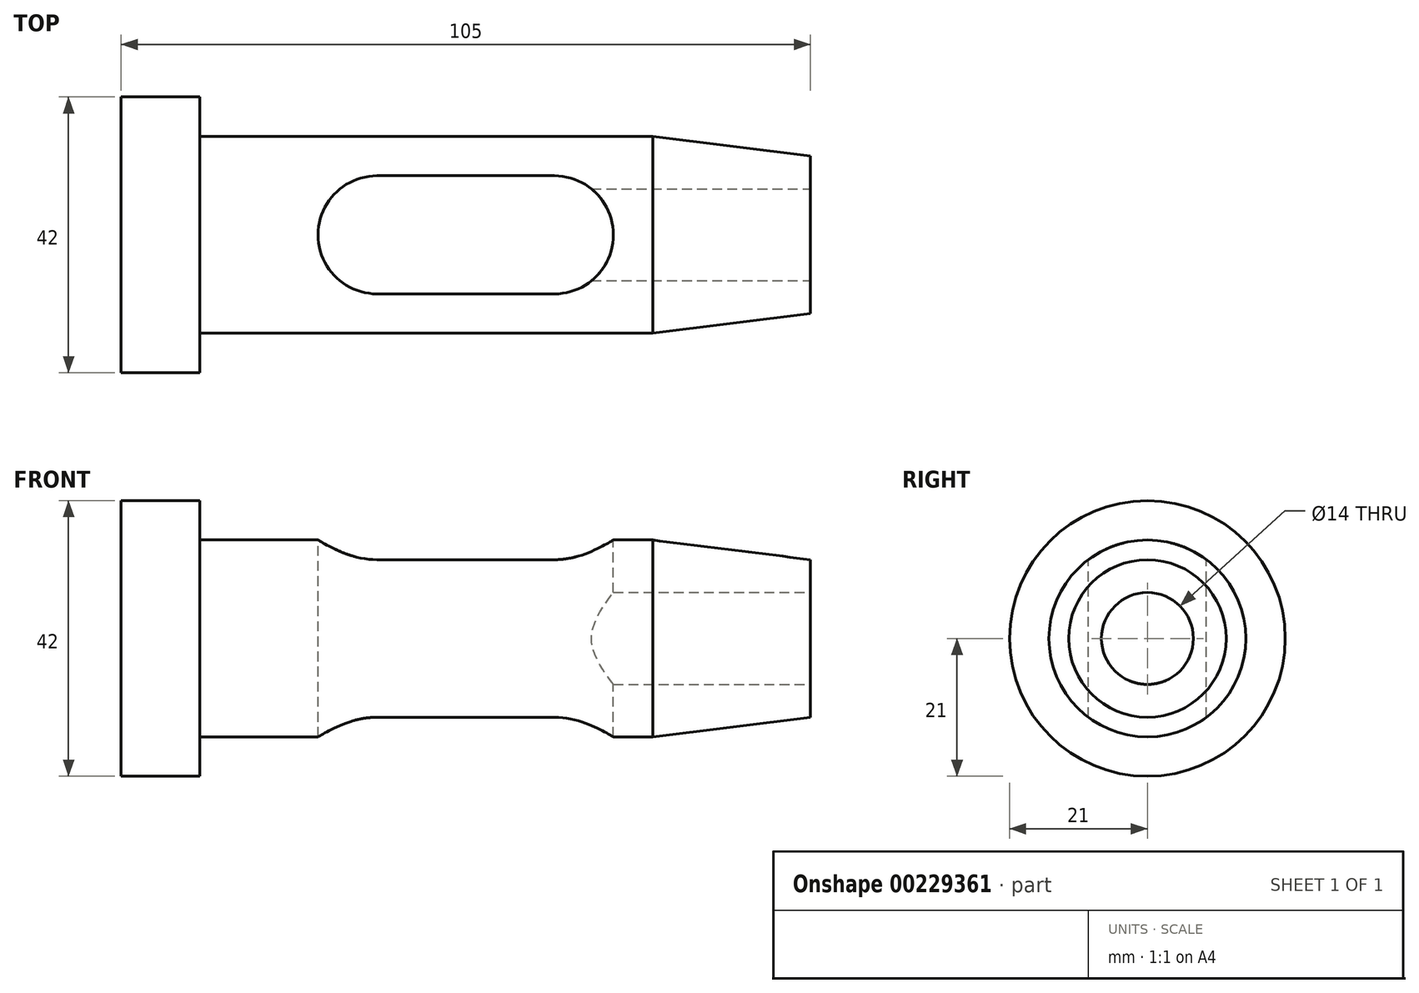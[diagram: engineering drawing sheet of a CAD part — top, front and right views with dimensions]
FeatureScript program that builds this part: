
annotation { "Feature Type Name" : "Feature", "Feature Type Description" : "" }
export const myFeature = defineFeature(function(context is Context, id is Id, definition is map)
    precondition{}
    {
        {
            var Q0;
            Q0=qCreatedBy(makeId("Front.planeOp"),FACE);
            var sketch = newSketch(context, id + "F0", { "sketchPlane" : qUnion([Q0])});
            skLineSegment(sketch, "E0", {"start": v(-105, 0) * mm, "end": v(0, 0) * mm, "construction": true});
            skLineSegment(sketch, "E1", {"start": v(-105, 0) * mm, "end": v(-105, 21) * mm});
            skLineSegment(sketch, "E2", {"start": v(-105, 21) * mm, "end": v(-93, 21) * mm});
            skLineSegment(sketch, "E3", {"start": v(-93, 21) * mm, "end": v(-93, 15) * mm});
            skLineSegment(sketch, "E4", {"start": v(-93, 15) * mm, "end": v(-24, 15) * mm});
            skLineSegment(sketch, "E5", {"start": v(-24, 15) * mm, "end": v(0, 12) * mm});
            skLineSegment(sketch, "E6", {"start": v(0, 12) * mm, "end": v(0, 0) * mm});
            skLineSegment(sketch, "E7", {"start": v(-105, 0) * mm, "end": v(0, 0) * mm});
            skSolve(sketch);
        }
        {
            var Q0;
            Q0 = qSketchRegion(id + "F0", true);
            var Q1;
            Q1=sQuery(id+"F0.wireOp",EDGE,"E7");
            revolve(context, id + "F1", {"entities" : qUnion([Q0]), "axis" : qUnion([Q1]), "revolveType" : RevolveType.FULL});
        }
        {
            var Q0;
            Q0=qCreatedBy(makeId("Top.planeOp"),FACE);
            var sketch = newSketch(context, id + "F2", { "sketchPlane" : qUnion([Q0])});
            skLineSegment(sketch, "E8", {"start": v(-39, 0) * mm, "end": v(-66, 0) * mm, "construction": true});
            skArc(sketch, "E9.0.startCap", {"start": v(-39, 9) * mm, "mid": v(-30, 0) * mm, "end": v(-39, -9) * mm});
            skArc(sketch, "E9.0.endCap", {"start": v(-66, -9) * mm, "mid": v(-75, 0) * mm, "end": v(-66, 9) * mm});
            skLineSegment(sketch, "E9.0.left", {"start": v(-39, -9) * mm, "end": v(-66, -9) * mm});
            skLineSegment(sketch, "E9.0.right", {"start": v(-39, 9) * mm, "end": v(-66, 9) * mm});
            skSolve(sketch);
        }
        {
            var Q0;
            Q0 = qSketchRegion(id + "F2", true);
            extrude(context, id + "F3", {"entities" : qUnion([Q0]), "operationType" : NewBodyOperationType.REMOVE, "endBound" : BoundingType.THROUGH_ALL, "oppositeDirection" : true, "depth" : 25 * mm, "hasSecondDirection" : true, "secondDirectionBound" : SecondDirectionBoundingType.THROUGH_ALL, "secondDirectionOppositeDirection" : false, "secondDirectionDepth" : 25 * mm});
        }
        {
            var Q0;
            Q0=makeQuery(id+"F1.opRevolve","SWEPT_FACE",FACE,{"disambiguationData":[OSD([sQuery(id+"F0.wireOp",EDGE,"E6")])]});
            var sketch = newSketch(context, id + "F4", { "sketchPlane" : qUnion([Q0])});
            skPoint(sketch, "E10", {"position": v(0, 0) * mm});
            skCircle(sketch, "E11", {"center": v(0, 0) * mm, "radius": 7 * mm});
            skSolve(sketch);
        }
        {
            var Q0;
            Q0 = qSketchRegion(id + "F4", true);
            var Q1;
            Q1=makeQuery(id+"F3.boolean.opBoolean","COPY",FACE,{"derivedFrom":makeQuery(id+"F3.opExtrude","SWEPT_FACE",FACE,{"disambiguationData":[OSD([sQuery(id+"F2.wireOp",EDGE,"E9.0.startCap")])]})});
            extrude(context, id + "F5", {"entities" : qUnion([Q0]), "operationType" : NewBodyOperationType.REMOVE, "endBound" : BoundingType.UP_TO_SURFACE, "oppositeDirection" : true, "endBoundEntityFace" : qUnion([Q1]), "depth" : 25 * mm});
        }
    });
